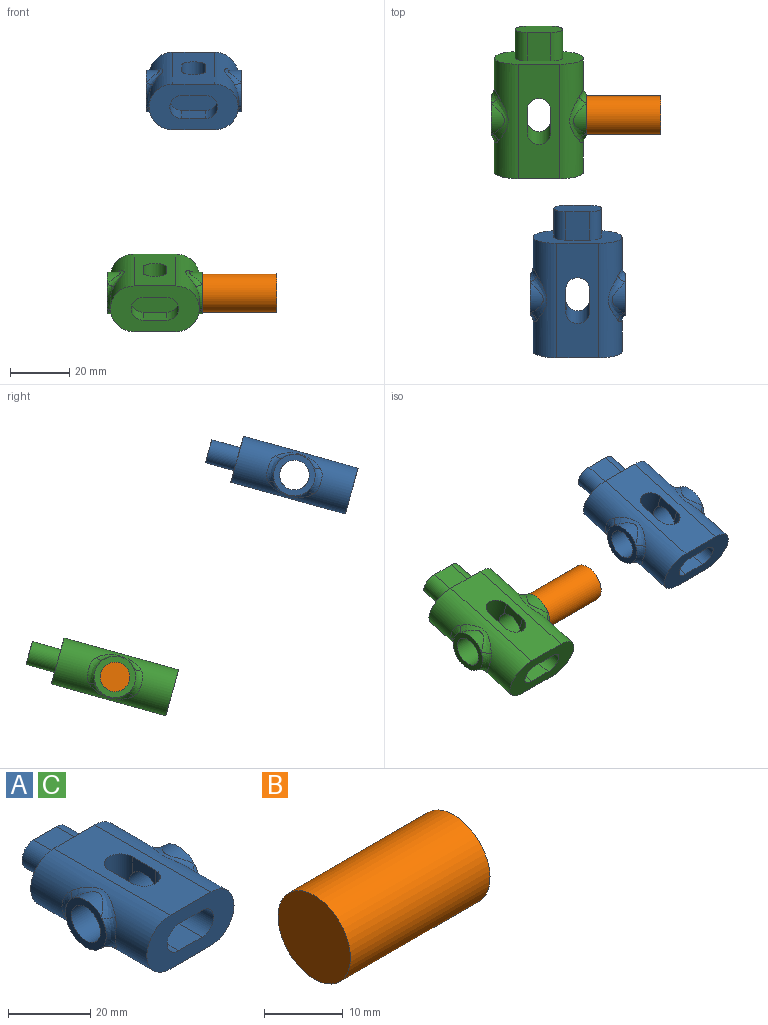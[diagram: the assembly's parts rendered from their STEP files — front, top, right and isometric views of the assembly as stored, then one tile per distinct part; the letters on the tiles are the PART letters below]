
ASSEMBLY  parts=3 mates=2
PART A: 38 faces, bbox 34.1x50.3x16.3 mm
  f0: cylinder r=7mm len=10.84mm, axis (-1,0,0), area 31.8mm2, adj f15,f35
  f1: cylinder r=7mm len=10.84mm, axis (-1,0,0), area 31.8mm2, adj f18,f31
  f2: plane 30x16mm, normal (0,1,0), area 310.8mm2, adj f5,f6,f11,f12,f25,f26,f28,f29
  f3: plane 30x16mm, normal (0,-1,0), area 310.8mm2, adj f5,f6,f11,f12,f20,f21,f23,f24
  f4: cylinder r=5mm len=12mm, axis (1,0,0), area 377mm2, adj f7,f9,f10,f13,f18
  f5: cylinder r=8mm len=40mm, axis (0,1,0), area 746.6mm2, adj f2,f3,f11,f12,f30,f31,f32,f33
  f6: cylinder r=8mm len=40mm, axis (0,-1,0), area 746.6mm2, adj f2,f3,f11,f12,f34,f35,f36,f37
  f7: plane 8x5mm, normal (1,0,0), area 28.8mm2, adj f4,f9,f10,f12
  f8: plane 8x5mm, normal (-1,0,0), area 28.8mm2, adj f9,f10,f12,f19
  f9: cylinder r=4mm len=16mm, axis (0,0,1), area 192.8mm2, adj f4,f7,f8,f11,f12,f13,f14,f19
  f10: cylinder r=4mm len=16mm, axis (0,0,-1), area 192.8mm2, adj f4,f7,f8,f11,f12,f13,f14,f19
  f11: plane 40x14mm, normal (0,0,1), area 445.7mm2, adj f2,f3,f5,f6,f9,f10,f13,f14
  f12: plane 40x14mm, normal (0,0,-1), area 445.7mm2, adj f2,f3,f5,f6,f7,f8,f9,f10
  f13: plane 8x5mm, normal (1,0,0), area 28.8mm2, adj f4,f9,f10,f11
  f14: plane 8x5mm, normal (-1,0,0), area 28.8mm2, adj f9,f10,f11,f19
  f15: plane 14.31x14.31mm, normal (1,0,0), area 75.4mm2, adj f0,f16,f19,f34,f37
  f16: cylinder r=7mm len=10.84mm, axis (-1,0,0), area 31.8mm2, adj f15,f36
  f17: cylinder r=7mm len=10.84mm, axis (-1,0,0), area 31.8mm2, adj f18,f32
  f18: plane 14.31x14.31mm, normal (-1,0,0), area 75.4mm2, adj f1,f4,f17,f30,f33
  f19: cylinder r=5mm len=12mm, axis (1,0,0), area 377mm2, adj f8,f9,f10,f14,f15
  f20: plane 10x8mm, normal (0,0,-1), area 80mm2, adj f3,f22,f23,f24
  f21: plane 10x8mm, normal (0,0,1), area 80mm2, adj f3,f22,f23,f24
  f22: plane 16x8mm, normal (0,-1,0), area 114.3mm2, adj f20,f21,f23,f24
  f23: cylinder r=4mm len=10mm, axis (0,1,0), area 125.7mm2, adj f3,f20,f21,f22
  f24: cylinder r=4mm len=10mm, axis (0,1,0), area 125.7mm2, adj f3,f20,f21,f22
  f25: plane 10x8mm, normal (0,0,1), area 80mm2, adj f2,f27,f28,f29
  f26: plane 10x8mm, normal (0,0,-1), area 80mm2, adj f2,f27,f28,f29
  f27: plane 16x8mm, normal (0,1,0), area 114.3mm2, adj f25,f26,f28,f29
  f28: cylinder r=4mm len=10mm, axis (0,-1,0), area 125.7mm2, adj f2,f25,f26,f27
  f29: cylinder r=4mm len=10mm, axis (0,-1,0), area 125.7mm2, adj f2,f25,f26,f27
  f30: bspline ~10.12x4.43mm, area 27.6mm2, adj f5,f18,f31,f32
  f31: bspline ~17.22x6.58mm, area 37.4mm2, adj f1,f5,f30,f33
  f32: bspline ~15.49x5.67mm, area 37.4mm2, adj f5,f17,f30,f33
  f33: bspline ~10.12x4.43mm, area 27.6mm2, adj f5,f18,f31,f32
  f34: bspline ~10.12x4.43mm, area 27.6mm2, adj f6,f15,f35,f36
  f35: bspline ~17.22x6.58mm, area 37.4mm2, adj f0,f6,f34,f37
  f36: bspline ~15.49x5.67mm, area 37.4mm2, adj f6,f16,f34,f37
  f37: bspline ~10.12x4.43mm, area 27.6mm2, adj f6,f15,f35,f36
PART B: 3 faces, bbox 25x13x13 mm
  f0: cylinder r=6.48mm len=25mm, axis (-1,0,0), area 1018.1mm2, adj f1,f2
  f1: plane 12.96x12.96mm, normal (1,0,0), area 132mm2, adj f0
  f2: plane 12.96x12.96mm, normal (-1,0,0), area 132mm2, adj f0
PART C: same geometry as A
PLACE A rot(axis=(1,0,0),15.6deg) t=(-2.64,-109.44,99.74)mm
PLACE B t=(-22.15,-119.77,-21.2)mm
PLACE C rot(axis=(1,0,0),15.6deg) t=(-15.69,-48.98,31.77)mm
MATE revolute B.f0 <-> C.f0  axis (-1,0,0) through (-22.15,-65.79,27.09)mm
MATE planar C.f3 <-> A.f2  axis (0,-0.96,-0.27) through (-38.15,-85.06,21.72)mm
